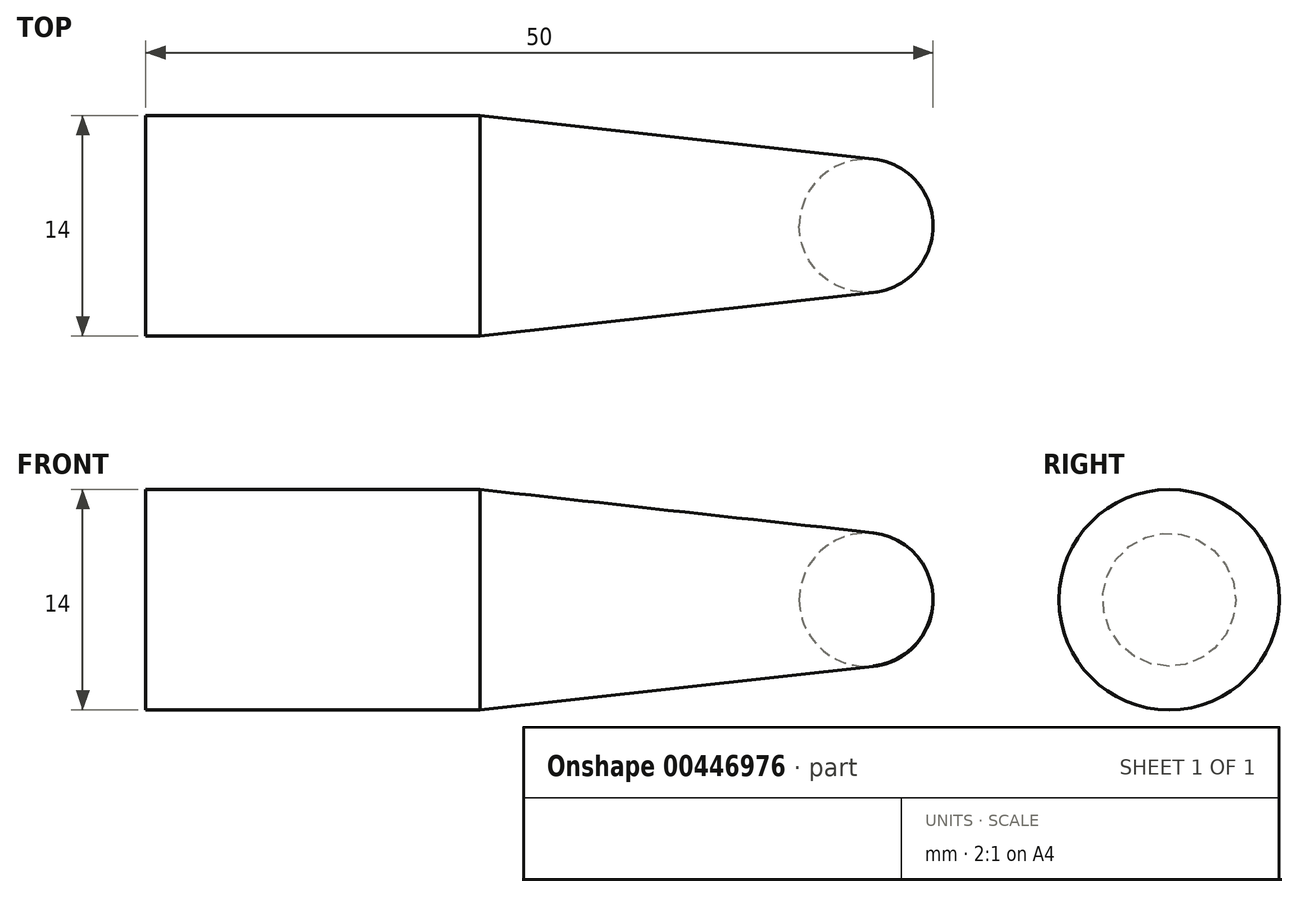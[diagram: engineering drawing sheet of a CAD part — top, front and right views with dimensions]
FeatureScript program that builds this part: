
annotation { "Feature Type Name" : "Feature", "Feature Type Description" : "" }
export const myFeature = defineFeature(function(context is Context, id is Id, definition is map)
    precondition{}
    {
        {
            var Q0;
            Q0=qCreatedBy(makeId("Front.planeOp"),FACE);
            var sketch = newSketch(context, id + "F0", { "sketchPlane" : qUnion([Q0])});
            skLineSegment(sketch, "E0", {"start": v(0, 0) * mm, "end": v(0, 7) * mm});
            skLineSegment(sketch, "E1", {"start": v(0, 7) * mm, "end": v(21.21, 7) * mm});
            skLineSegment(sketch, "E2", {"start": v(21.21, 7) * mm, "end": v(46.21, 4.25) * mm});
            skArc(sketch, "E3", {"start": v(50, 0) * mm, "mid": v(48.92, 2.85) * mm, "end": v(46.21, 4.25) * mm});
            skLineSegment(sketch, "E4", {"start": v(50, 0) * mm, "end": v(0, 0) * mm});
            skLineSegment(sketch, "E5", {"start": v(0, 0) * mm, "end": v(34.31, 0) * mm});
            skSolve(sketch);
        }
        {
            var Q0;
            Q0 = qSketchRegion(id + "F0", true);
            var Q1;
            Q1=sQuery(id+"F0.wireOp",EDGE,"E5");
            revolve(context, id + "F1", {"entities" : qUnion([Q0]), "axis" : qUnion([Q1]), "revolveType" : RevolveType.FULL});
        }
    });
